# Revit family: Hager-Vega_D-IP30-vazio-PT-pt
name_source: partatom
category: Electrical Equipment
units: mm (PartAtom-declared; Revit-internal decimal feet)

## family parameters
Cut with Voids When Loaded = No
Host = Face
Panel Configuration = Two Columns, Circuits Across
Part Type = Panelboard
Room Calculation Point = No
Round Connector Dimension = Use Diameter
Shared = No

## types (1)
- Montagem embutida IP30 L600 A537 P182 24 unidade de divisão - FU22AN
    Default Elevation = 0 mm  [stored 0 ft]
    EF000003 - Método de montagem = EV000383 - Montagem embutida (gesso)
    EF000007 - Cor = EV000202 - Branco
    EF000008 - Largura = 600 mm
    EF000040 - Altura = 537 mm  [stored 1.76181 ft]
    EF000049 - Profundidade = 182 mm  [stored 0.597113 ft]
    EF000116 - Número RAL = 9010
    EF000118 - Com tampa de montagem = No
    EF000218 - Profundidade incorporada = 110 mm  [stored 0.360892 ft]
    EF000266 - Número de linhas = 0
    EF000332 - Altura embutida = 537 mm  [stored 1.76181 ft]
    EF000339 - Tipo de difusor = EV000494 - Nenhum
    EF000846 - Largura para embutir = 600 mm
    EF001062 - Versão EMC = No
    EF001088 - Extensão possível = Yes
    EF001131 - Profundidade interior = 110 mm  [stored 0.360892 ft]
    EF001134 - Calha DIN = Yes
    EF001596 - Material do corpo = EV000154 - Outro
    EF002950 - Largura em número de módulos = 24
    EF005474 - Grau de proteção (IP) = EV006410 - IP30
    EF006244 - Tampa/porta transparente = No
    EF006306 - Com fecho = No
    EF009212 - Tipo de tampa = EV009916 - Com recuo
    EF015776 - Borne de terra = No
    EF015777 - Borne de neutro = No
    EF015941 - Porta para passagem de sinal = No
    HG000001 - Número de colunas = 0
    HG000002 - Com porta ou tampa = No
    HG000003 - Gama = Vega D
    HG000004 - Referência do Fabricante = FU22AN
    HG000005 - Espessura = 3 mm  [stored 0.00984252 ft]
    HG000006 - Encastrado = Yes
    HG000007 - Número de colunas vazias = 0
    HG000008 - Número de filas vazias = 0
    HG000009 - Porta dupla = No
    HG000010 - Portas assimétricas = No
    HG000011 - Filas vazias desde da parte de baixo = No
    HG000017 - Distância entre polos = 18 mm  [stored 0.0590551 ft]
    Manufacturer = Hager
    Model = FU22AN
    Type Comments = Vega D

note: [stored X ft] marks values corroborated as IEEE doubles in the binary element streams (Revit-internal decimal feet)

## geometry (parser evidence)
native form markers: Sweep x16
no freeform markers — native parametric forms only
